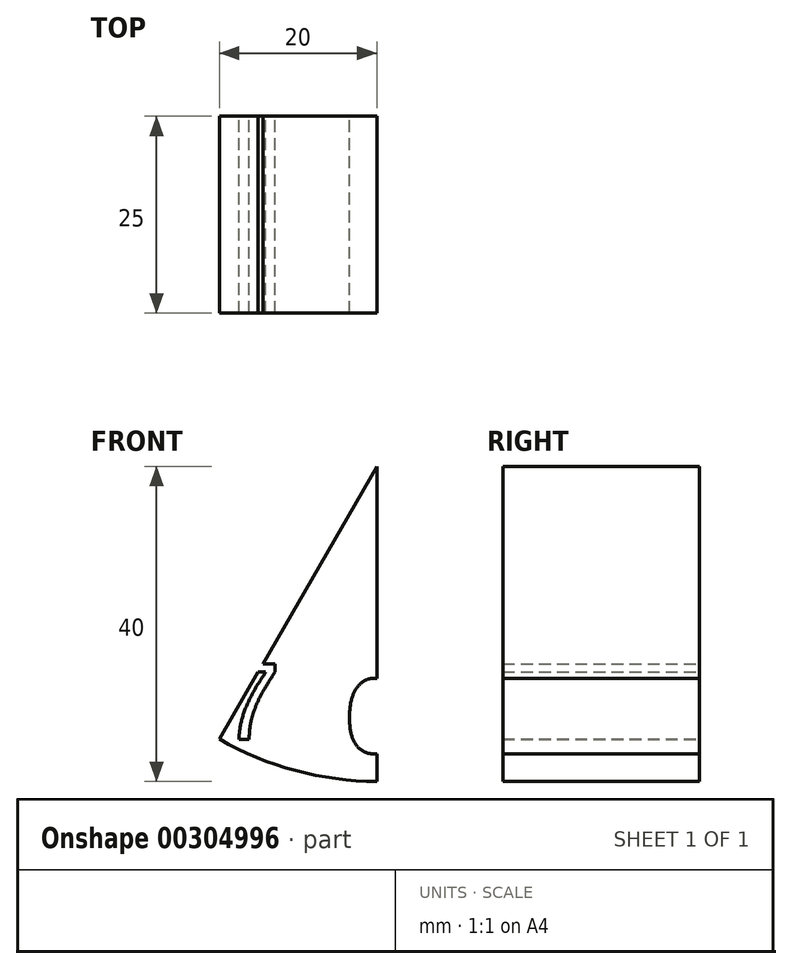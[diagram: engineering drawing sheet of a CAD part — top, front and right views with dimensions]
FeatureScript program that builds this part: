
annotation { "Feature Type Name" : "Feature", "Feature Type Description" : "" }
export const myFeature = defineFeature(function(context is Context, id is Id, definition is map)
    precondition{}
    {
        {
            var Q0;
            Q0=qCreatedBy(makeId("Front.planeOp"),FACE);
            var sketch = newSketch(context, id + "F0", { "sketchPlane" : qUnion([Q0])});
            skCircle(sketch, "E0", {"center": v(0, 0) * mm, "radius": 40 * mm});
            skCircle(sketch, "E1", {"center": v(0, 0) * mm, "radius": 41.5 * mm});
            skLineSegment(sketch, "E2", {"start": v(0, 0) * mm, "end": v(20, 34.64) * mm});
            skLineSegment(sketch, "E3", {"start": v(0, 0) * mm, "end": v(34.64, 20) * mm});
            skLineSegment(sketch, "E4", {"start": v(0, 0) * mm, "end": v(40, 0) * mm});
            skLineSegment(sketch, "E5", {"start": v(0, 0) * mm, "end": v(34.64, -20) * mm});
            skLineSegment(sketch, "E6", {"start": v(0, 0) * mm, "end": v(20, -34.64) * mm});
            skLineSegment(sketch, "E7", {"start": v(0, 0) * mm, "end": v(0, -40) * mm});
            skLineSegment(sketch, "E8.MirrorCS", {"start": v(0, 0) * mm, "end": v(-20, 34.64) * mm});
            skLineSegment(sketch, "E9.MirrorCS", {"start": v(0, 0) * mm, "end": v(-34.64, 20) * mm});
            skLineSegment(sketch, "E10.MirrorCS", {"start": v(0, 0) * mm, "end": v(-34.64, -20) * mm});
            skLineSegment(sketch, "E11.MirrorCS", {"start": v(0, 0) * mm, "end": v(-20, -34.64) * mm});
            skLineSegment(sketch, "E12.MirrorCS", {"start": v(0, 0) * mm, "end": v(-40, 0) * mm});
            skText(sketch, "E13", { "text": "12", "fontName": "Arimo-Regular.ttf"});
            skText(sketch, "E14", { "text": "1", "fontName": "Arimo-Regular.ttf"});
            skText(sketch, "E15", { "text": "2", "fontName": "Arimo-Regular.ttf"});
            skText(sketch, "E16", { "text": "3", "fontName": "Arimo-Regular.ttf"});
            skLineSegment(sketch, "E17.MirrorCS", {"start": v(0, 0) * mm, "end": v(0, 40) * mm});
            skText(sketch, "E18", { "text": "4", "fontName": "Arimo-Regular.ttf"});
            skText(sketch, "E19", { "text": "5", "fontName": "Arimo-Regular.ttf"});
            skText(sketch, "E20", { "text": "6", "fontName": "Arimo-Regular.ttf"});
            skText(sketch, "E21", { "text": "7", "fontName": "Arimo-Regular.ttf"});
            skText(sketch, "E22", { "text": "8", "fontName": "Arimo-Regular.ttf"});
            skText(sketch, "E23", { "text": "9", "fontName": "Arimo-Regular.ttf"});
            skText(sketch, "E24", { "text": "10", "fontName": "Arimo-Regular.ttf"});
            skText(sketch, "E25", { "text": "11", "fontName": "Arimo-Regular.ttf"});
            const initialGuessF0  = {"E13": [-0.00635, 0.02933, 1, 0, 0.00803], "E14": [0.01014, 0.02237, 1, 0, 0.01205], "E15": [0.02285, 0.00996, 1, 0, 0.01252], "E16": [0.02909, -0.00509, 1, 0, 0.01157], "E18": [0.02284, -0.02413, 1, 0, 0.01094], "E19": [0.01228, -0.03464, 1, 0, 0.00952], "E20": [-0.00418, -0.0364, 1, 0, 0.0098], "E21": [-0.02, -0.0347, 1, 0, 0.01006], "E22": [-0.03307, -0.02346, 1, 0, 0.01028], "E23": [-0.03686, -0.00509, 1, 0, 0.01352], "E24": [-0.03498, 0.00996, 1, 0, 0.00943], "E25": [-0.02327, 0.0228, 1, 0, 0.00837]};
            skSetInitialGuess(sketch, initialGuessF0);
            skSolve(sketch);
        }
        {
            var Q0;
            Q0=makeQuery(id+"F0.imprint","IMPRINT",FACE,{"disambiguationData":[TD([[makeQuery(id+"F0.imprint","IMPRINT",EDGE,{"derivedFrom":sQuery(id+"F0.wireOp",EDGE,"E0")}),1.0]])]});
            extrude(context, id + "F1", {"entities" : qUnion([Q0]), "depth" : 25 * mm});
        }
        {
            var Q0;
            Q0=sQuery(id+"F0.wireOp",EDGE,"E1");
            extrude(context, id + "F2", {"bodyType" : ToolBodyType.SURFACE, "surfaceEntities" : qUnion([Q0]), "oppositeDirection" : true, "depth" : 2 * mm});
        }
    });
